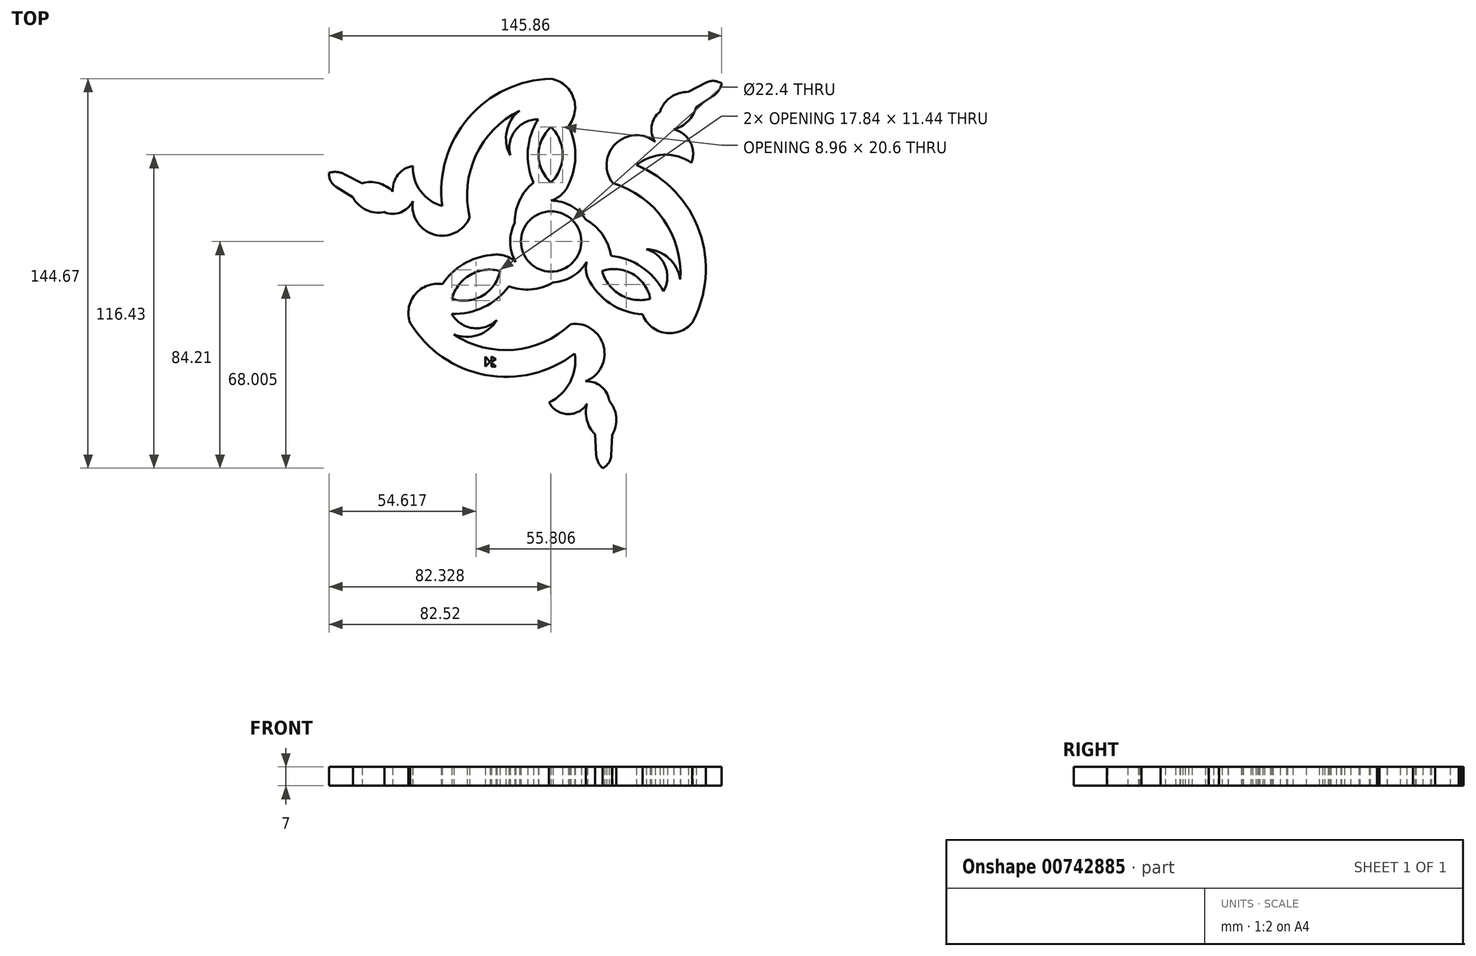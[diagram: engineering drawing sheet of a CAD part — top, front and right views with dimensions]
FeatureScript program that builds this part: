
annotation { "Feature Type Name" : "Feature", "Feature Type Description" : "" }
export const myFeature = defineFeature(function(context is Context, id is Id, definition is map)
    precondition{}
    {
        {
            var Q0;
            Q0=qCreatedBy(makeId("Top.planeOp"),FACE);
            var sketch = newSketch(context, id + "F0", { "sketchPlane" : qUnion([Q0])});
            skCircle(sketch, "E0", {"center": v(0, 0) * mm, "radius": 11.2 * mm});
            skArc(sketch, "E1", {"start": v(0, 50.9) * mm, "mid": v(-8.1, 37.5) * mm, "end": v(-6.53, 21.92) * mm});
            skArc(sketch, "E2.1.0", {"start": v(-44.08, -25.45) * mm, "mid": v(-28.43, -25.76) * mm, "end": v(-15.72, -16.62) * mm});
            skArc(sketch, "E2.2.0", {"start": v(44.08, -25.45) * mm, "mid": v(34.84, -10.32) * mm, "end": v(17.85, -5.24) * mm});
            skArc(sketch, "E3", {"start": v(6.8, 21.92) * mm, "mid": v(8.38, 37.58) * mm, "end": v(0, 50.9) * mm});
            skArc(sketch, "E4.1.0", {"start": v(-22.38, -5.08) * mm, "mid": v(-36.73, -11.53) * mm, "end": v(-44.08, -25.45) * mm});
            skArc(sketch, "E4.2.0", {"start": v(13.52, -13.34) * mm, "mid": v(26.43, -25.38) * mm, "end": v(44.08, -25.45) * mm});
            skArc(sketch, "E5", {"start": v(0, 42.52) * mm, "mid": v(-4.67, 32.22) * mm, "end": v(0, 21.92) * mm});
            skArc(sketch, "E6.1.0", {"start": v(-36.82, -21.26) * mm, "mid": v(-25.57, -20.16) * mm, "end": v(-18.98, -10.96) * mm});
            skArc(sketch, "E6.2.0", {"start": v(36.82, -21.26) * mm, "mid": v(30.24, -12.06) * mm, "end": v(18.98, -10.96) * mm});
            skArc(sketch, "E7", {"start": v(0, 21.92) * mm, "mid": v(4.29, 32.22) * mm, "end": v(0, 42.52) * mm});
            skArc(sketch, "E8.1.0", {"start": v(-18.98, -10.96) * mm, "mid": v(-30.05, -12.4) * mm, "end": v(-36.82, -21.26) * mm});
            skArc(sketch, "E8.2.0", {"start": v(18.98, -10.96) * mm, "mid": v(25.76, -19.82) * mm, "end": v(36.82, -21.26) * mm});
            skArc(sketch, "E9", {"start": v(-4.8, 45.38) * mm, "mid": v(-13.3, 41.29) * mm, "end": v(-15.2, 32.05) * mm});
            skArc(sketch, "E10.1.0", {"start": v(-36.9, -26.86) * mm, "mid": v(-29.1, -32.17) * mm, "end": v(-20.16, -29.2) * mm});
            skArc(sketch, "E10.2.0", {"start": v(41.7, -18.53) * mm, "mid": v(42.4, -9.12) * mm, "end": v(35.36, -2.86) * mm});
            skArc(sketch, "E11", {"start": v(0, 50.9) * mm, "mid": v(-13.86, 46.53) * mm, "end": v(-15.2, 32.05) * mm});
            skArc(sketch, "E12.1.0", {"start": v(-44.08, -25.45) * mm, "mid": v(-33.36, -35.27) * mm, "end": v(-20.16, -29.2) * mm});
            skArc(sketch, "E12.2.0", {"start": v(44.08, -25.45) * mm, "mid": v(47.22, -11.26) * mm, "end": v(35.36, -2.86) * mm});
            skArc(sketch, "E13", {"start": v(-3.64, 51.42) * mm, "mid": v(-25.9, 35.82) * mm, "end": v(-30.22, 8.99) * mm});
            skArc(sketch, "E14.1.0", {"start": v(-42.7, -28.86) * mm, "mid": v(-18.07, -40.33) * mm, "end": v(7.33, -30.66) * mm});
            skArc(sketch, "E14.2.0", {"start": v(46.35, -22.56) * mm, "mid": v(43.97, 4.52) * mm, "end": v(22.9, 21.68) * mm});
            skArc(sketch, "E15", {"start": v(-51.38, 14.95) * mm, "mid": v(-43.45, 2.57) * mm, "end": v(-30.22, 8.99) * mm});
            skArc(sketch, "E16.1.0", {"start": v(12.74, -51.97) * mm, "mid": v(19.5, -38.91) * mm, "end": v(7.33, -30.66) * mm});
            skArc(sketch, "E16.2.0", {"start": v(38.64, 37.02) * mm, "mid": v(23.95, 36.34) * mm, "end": v(22.9, 21.68) * mm});
            skArc(sketch, "E17", {"start": v(-61.95, 10.88) * mm, "mid": v(-55.87, 10.84) * mm, "end": v(-51.38, 14.95) * mm});
            skArc(sketch, "E18.1.0", {"start": v(21.55, -59.1) * mm, "mid": v(18.55, -53.8) * mm, "end": v(12.74, -51.97) * mm});
            skArc(sketch, "E18.2.0", {"start": v(40.4, 48.21) * mm, "mid": v(37.32, 42.96) * mm, "end": v(38.64, 37.02) * mm});
            skArc(sketch, "E19", {"start": v(-73.62, 16.34) * mm, "mid": v(-68.67, 11.72) * mm, "end": v(-61.95, 10.88) * mm});
            skArc(sketch, "E20.1.0", {"start": v(22.66, -71.93) * mm, "mid": v(24.19, -65.33) * mm, "end": v(21.55, -59.1) * mm});
            skArc(sketch, "E20.2.0", {"start": v(50.97, 55.59) * mm, "mid": v(44.49, 53.61) * mm, "end": v(40.4, 48.21) * mm});
            skLineSegment(sketch, "E21", {"start": v(-73.62, 16.34) * mm, "end": v(-79.93, 20.35) * mm});
            skLineSegment(sketch, "E22.1.0", {"start": v(22.66, -71.93) * mm, "end": v(22.34, -79.4) * mm});
            skLineSegment(sketch, "E22.2.0", {"start": v(50.97, 55.59) * mm, "end": v(57.59, 59.04) * mm});
            skArc(sketch, "E23", {"start": v(-82.5, 25.51) * mm, "mid": v(-81.93, 22.57) * mm, "end": v(-79.93, 20.35) * mm});
            skArc(sketch, "E24.1.0", {"start": v(19.16, -84.2) * mm, "mid": v(21.41, -82.24) * mm, "end": v(22.34, -79.4) * mm});
            skArc(sketch, "E24.2.0", {"start": v(63.34, 58.7) * mm, "mid": v(60.52, 59.67) * mm, "end": v(57.59, 59.04) * mm});
            skArc(sketch, "E25", {"start": v(0, 60.46) * mm, "mid": v(-30.76, 45.87) * mm, "end": v(-40.44, 13.23) * mm});
            skArc(sketch, "E26.1.0", {"start": v(-52.36, -30.23) * mm, "mid": v(-24.34, -49.58) * mm, "end": v(8.77, -41.64) * mm});
            skArc(sketch, "E26.2.0", {"start": v(52.36, -30.23) * mm, "mid": v(55.1, 3.7) * mm, "end": v(31.68, 28.41) * mm});
            skArc(sketch, "E27", {"start": v(6.44, 42.91) * mm, "mid": v(8.25, 53.54) * mm, "end": v(0, 60.46) * mm});
            skArc(sketch, "E28.1.0", {"start": v(-40.39, -15.88) * mm, "mid": v(-50.5, -19.62) * mm, "end": v(-52.36, -30.23) * mm});
            skArc(sketch, "E28.2.0", {"start": v(33.94, -27.04) * mm, "mid": v(42.24, -33.92) * mm, "end": v(52.36, -30.23) * mm});
            skArc(sketch, "E29.1.0", {"start": v(-0.76, -59.76) * mm, "mid": v(7.01, -52.28) * mm, "end": v(8.77, -41.64) * mm});
            skArc(sketch, "E29.2.0", {"start": v(52.13, 29.22) * mm, "mid": v(41.77, 32.21) * mm, "end": v(31.68, 28.41) * mm});
            skArc(sketch, "E30", {"start": v(-51.38, 28.08) * mm, "mid": v(-48.5, 18.75) * mm, "end": v(-40.44, 13.23) * mm});
            skArc(sketch, "E31", {"start": v(-51.38, 28.08) * mm, "mid": v(-56.9, 24.75) * mm, "end": v(-58.85, 18.6) * mm});
            skArc(sketch, "E32", {"start": v(-0.76, -59.76) * mm, "mid": v(6.13, -64.14) * mm, "end": v(13.31, -60.27) * mm});
            skArc(sketch, "E33", {"start": v(52.13, 29.22) * mm, "mid": v(51.67, 36.94) * mm, "end": v(45.54, 41.67) * mm});
            skArc(sketch, "E34", {"start": v(-58.85, 18.6) * mm, "mid": v(-64.1, 21.7) * mm, "end": v(-70.2, 21.67) * mm});
            skArc(sketch, "E35.1.0", {"start": v(13.31, -60.27) * mm, "mid": v(13.27, -66.37) * mm, "end": v(16.34, -71.63) * mm});
            skArc(sketch, "E35.2.0", {"start": v(45.54, 41.67) * mm, "mid": v(50.84, 44.67) * mm, "end": v(53.86, 49.96) * mm});
            skLineSegment(sketch, "E36", {"start": v(-70.2, 21.67) * mm, "end": v(-76.92, 25.08) * mm});
            skLineSegment(sketch, "E37.1.0", {"start": v(16.34, -71.63) * mm, "end": v(16.74, -79.15) * mm});
            skLineSegment(sketch, "E37.2.0", {"start": v(53.86, 49.96) * mm, "end": v(60.18, 54.07) * mm});
            skArc(sketch, "E38", {"start": v(-76.92, 25.08) * mm, "mid": v(-79.67, 25.85) * mm, "end": v(-82.5, 25.51) * mm});
            skArc(sketch, "E39.1.0", {"start": v(16.74, -79.15) * mm, "mid": v(17.45, -81.92) * mm, "end": v(19.16, -84.2) * mm});
            skArc(sketch, "E39.2.0", {"start": v(60.18, 54.07) * mm, "mid": v(62.22, 56.07) * mm, "end": v(63.34, 58.7) * mm});
            skPoint(sketch, "E40.endSnap0", {"position": v(-73.56, 23.37) * mm});
            skCircle(sketch, "E41", {"center": v(0, 0) * mm, "radius": 15.2 * mm});
            skPoint(sketch, "E42.orphan", {"position": v(0, 13.2) * mm});
            skPoint(sketch, "E43.orphan", {"position": v(-11.43, -6.6) * mm});
            skPoint(sketch, "E44.orphan", {"position": v(11.43, -6.6) * mm});
            skArc(sketch, "E45", {"start": v(-6.53, 21.92) * mm, "mid": v(-4.09, 17.76) * mm, "end": v(0, 15.2) * mm});
            skArc(sketch, "E46", {"start": v(0, 15.2) * mm, "mid": v(4.2, 17.75) * mm, "end": v(6.8, 21.92) * mm});
            skArc(sketch, "E47.1.0", {"start": v(-13.16, -7.6) * mm, "mid": v(-17.47, -5.24) * mm, "end": v(-22.38, -5.08) * mm});
            skArc(sketch, "E47.1.1", {"start": v(-15.72, -16.62) * mm, "mid": v(-13.34, -12.42) * mm, "end": v(-13.16, -7.6) * mm});
            skArc(sketch, "E47.2.0", {"start": v(13.16, -7.6) * mm, "mid": v(12.95, -10.5) * mm, "end": v(13.52, -13.34) * mm});
            skArc(sketch, "E47.2.1", {"start": v(17.85, -5.24) * mm, "mid": v(15.35, -6.11) * mm, "end": v(13.16, -7.6) * mm});
            skPoint(sketch, "E48.orphan", {"position": v(22.25, -5.3) * mm});
            skPoint(sketch, "E49.orphan", {"position": v(15.59, -16.84) * mm});
            skArc(sketch, "E50", {"start": v(-6.53, 21.92) * mm, "mid": v(-11.75, 15.24) * mm, "end": v(-13.51, 6.96) * mm});
            skArc(sketch, "E51.1.0", {"start": v(-15.72, -16.62) * mm, "mid": v(-7.33, -17.8) * mm, "end": v(0.73, -15.18) * mm});
            skArc(sketch, "E51.2.0", {"start": v(22.25, -5.3) * mm, "mid": v(19.07, 2.55) * mm, "end": v(12.78, 8.23) * mm});
            skLineSegment(sketch, "E52", {"start": v(-24.44, -42.82) * mm, "end": v(-24.44, -46.44) * mm});
            skLineSegment(sketch, "E53", {"start": v(-24.44, -46.44) * mm, "end": v(-24.44, -42.82) * mm});
            skLineSegment(sketch, "E54", {"start": v(-24.44, -42.82) * mm, "end": v(-22.7, -44.63) * mm});
            skPoint(sketch, "E54.endSnap0", {"position": v(-24.44, -44.63) * mm});
            skLineSegment(sketch, "E55", {"start": v(-22.7, -44.63) * mm, "end": v(-24.44, -46.44) * mm});
            skPoint(sketch, "E56.endSnap0", {"position": v(-22.22, -44.63) * mm});
            skLineSegment(sketch, "E57", {"start": v(-22.22, -42.82) * mm, "end": v(-22.22, -44.63) * mm});
            skLineSegment(sketch, "E58", {"start": v(-22.22, -44.95) * mm, "end": v(-22.22, -46.44) * mm});
            skLineSegment(sketch, "E59", {"start": v(-22.22, -46.44) * mm, "end": v(-20.48, -46.44) * mm});
            skLineSegment(sketch, "E60", {"start": v(-20.48, -46.44) * mm, "end": v(-22.22, -44.95) * mm});
            skLineSegment(sketch, "E61", {"start": v(-22.22, -42.82) * mm, "end": v(-20.48, -43.72) * mm});
            skPoint(sketch, "E61.endSnap0", {"position": v(-22.22, -43.72) * mm});
            skLineSegment(sketch, "E62", {"start": v(-20.48, -43.72) * mm, "end": v(-22.22, -44.63) * mm});
            skSolve(sketch);
        }
        {
            var Q0;
            Q0 = qSketchRegion(id + "F0", true);
            extrude(context, id + "F1", {"entities" : qUnion([Q0]), "depth" : 7 * mm, "offsetDistance" : 25 * mm});
        }
    });
